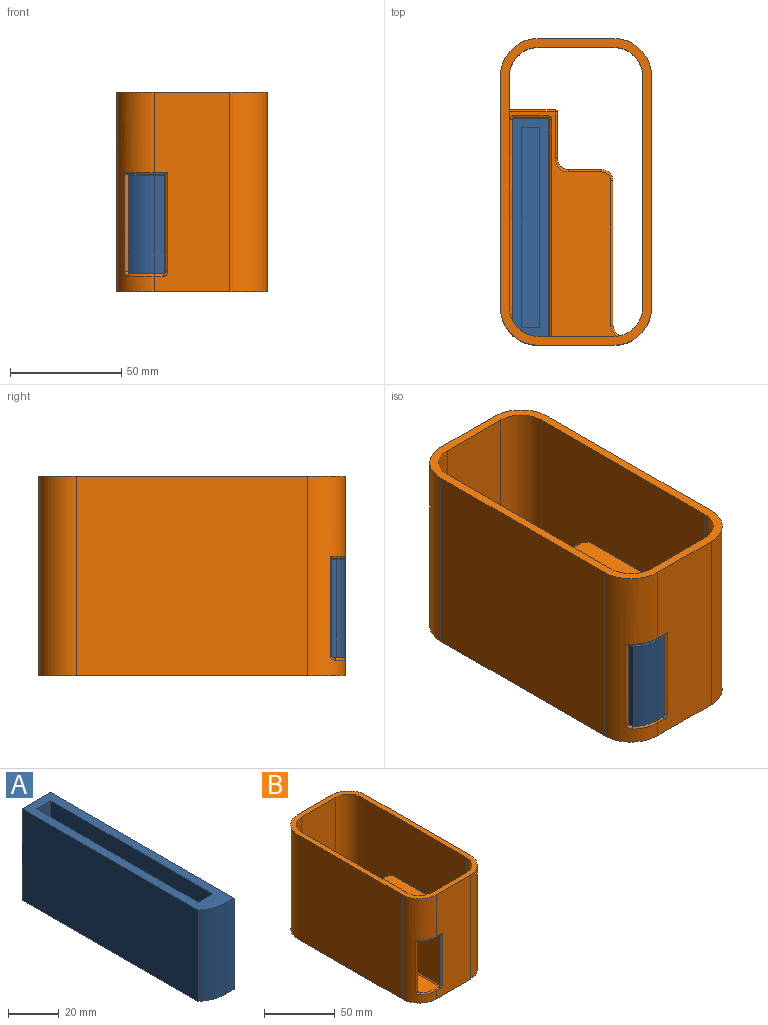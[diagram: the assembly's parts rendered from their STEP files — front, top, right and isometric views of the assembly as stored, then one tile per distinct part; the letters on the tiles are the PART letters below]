
ASSEMBLY  parts=2 mates=1
PART A: 13 faces, bbox 16x102x44 mm
  f0: plane 102x16mm, normal (0,0,1), area 896.4mm2, adj f2,f3,f4,f5,f7,f8,f9,f10
  f1: plane 102x16mm, normal (0,0,-1), area 1616.4mm2, adj f2,f3,f4,f5,f11,f12
  f2: plane 44x16mm, normal (0,1,0), area 704mm2, adj f0,f1,f4,f5
  f3: plane 44x0.43mm, normal (0,-1,0), area 18.9mm2, adj f0,f1,f5,f12
  f4: plane 102x44mm, normal (1,0,0), area 4488mm2, adj f0,f1,f2,f11
  f5: plane 98x44mm, normal (-1,0,0), area 4312mm2, adj f0,f1,f2,f3
  f6: plane 90x8mm, normal (0,0,1), area 720mm2, adj f7,f8,f9,f10
  f7: plane 40x8mm, normal (0,-1,0), area 320mm2, adj f0,f6,f9,f10
  f8: plane 40x8mm, normal (0,1,0), area 320mm2, adj f0,f6,f9,f10
  f9: plane 90x40mm, normal (-1,0,0), area 3600mm2, adj f0,f6,f7,f8
  f10: plane 90x40mm, normal (1,0,0), area 3600mm2, adj f0,f6,f7,f8
  f11: plane 44x4.62mm, normal (0,-1,0), area 203.1mm2, adj f0,f1,f4,f12
  f12: cylinder r=17mm len=44mm, axis (0,0,-1), area 523.8mm2, adj f0,f1,f3,f11
PART B: 81 faces, bbox 68.4x139.8x90.4 mm
  f0: plane 38.52x34mm, normal (0,1,0), area 1268.7mm2, adj f3,f4,f7,f20,f24,f40,f80
  f1: plane 101x50.48mm, normal (1,0,0), area 3978.9mm2, adj f2,f30,f31,f48,f49,f57
  f2: plane 36.48x25.38mm, normal (0,1,0), area 926.1mm2, adj f1,f20,f32,f67
  f3: plane 101x48.21mm, normal (0,0,1), area 2070.9mm2, adj f0,f4,f19,f20,f40,f43,f44,f45
  f4: cylinder r=13mm len=38.52mm, axis (0,0,-1), area 747.1mm2, adj f0,f3,f7,f19,f21,f43,f79
  f5: cylinder r=17mm len=90mm, axis (0,0,-1), area 1670mm2, adj f6,f7,f8,f13,f59,f60,f61,f63
  f6: plane 90x34mm, normal (0,-1,0), area 2779.3mm2, adj f5,f7,f8,f14,f62,f64,f65,f66
  f7: plane 138x68mm, normal (0,0,1), area 1481mm2, adj f0,f4,f5,f6,f9,f10,f11,f12
  f8: plane 138x68mm, normal (0,0,-1), area 3282.9mm2, adj f5,f6,f9,f10,f11,f12,f13,f14
  f9: plane 104x90mm, normal (1,0,0), area 9360mm2, adj f7,f8,f10,f14
  f10: cylinder r=17mm len=90mm, axis (0,0,-1), area 2403.3mm2, adj f7,f8,f9,f11
  f11: plane 90x34mm, normal (0,1,0), area 3060mm2, adj f7,f8,f10,f12
  f12: cylinder r=17mm len=90mm, axis (0,0,-1), area 2403.3mm2, adj f7,f8,f11,f13
  f13: plane 104x90mm, normal (-1,0,0), area 9360mm2, adj f5,f7,f8,f12
  f14: cylinder r=17mm len=90mm, axis (0,0,-1), area 2403.3mm2, adj f6,f7,f8,f9
  f15: plane 104x89mm, normal (-1,0,0), area 9256mm2, adj f7,f16,f20,f69
  f16: cylinder r=13mm len=89mm, axis (0,0,-1), area 1817.4mm2, adj f7,f15,f17,f70
  f17: plane 89x34mm, normal (0,-1,0), area 3026mm2, adj f7,f16,f18,f71
  f18: cylinder r=13mm len=89mm, axis (0,0,-1), area 1817.4mm2, adj f7,f17,f19,f72
  f19: plane 104x89mm, normal (1,0,0), area 4674.1mm2, adj f3,f4,f7,f18,f25,f47,f73
  f20: cylinder r=13mm len=89mm, axis (0,0,-1), area 1777.1mm2, adj f0,f2,f3,f7,f15,f32,f33,f52
  f21: plane 94.43x45.21mm, normal (1,0,0), area 3992.7mm2, adj f4,f22,f37,f42,f43,f61,f79
  f22: plane 17.17x8.44mm, normal (0,0,-1), area 37.4mm2, adj f21,f24,f61,f63,f65,f79,f80
  f23: plane 100.4x14.8mm, normal (0,0,1), area 1471.8mm2, adj f35,f36,f37,f60,f62
  f24: plane 100.4x44.8mm, normal (-1,0,0), area 4261.4mm2, adj f0,f22,f35,f40,f41,f66,f80
  f25: plane 50.48x20.62mm, normal (0,1,0), area 1040.7mm2, adj f19,f47,f49,f51
  f26: plane 42.4x14.8mm, normal (0,-1,0), area 627.5mm2, adj f36,f41,f42,f46
  f27: plane 65x8mm, normal (1,0,0), area 520mm2, adj f33,f34,f53,f75
  f28: plane 15x8mm, normal (0,1,0), area 120mm2, adj f30,f34,f55,f77
  f29: plane 69x19mm, normal (0,0,-1), area 1307.6mm2, adj f31,f32,f75,f76,f77
  f30: cylinder r=5mm len=14mm, axis (0,0,-1), area 80mm2, adj f1,f28,f56,f78
  f31: cylinder r=5mm len=80mm, axis (0,1,0), area 584mm2, adj f1,f29,f32,f78
  f32: cylinder r=5mm len=28.04mm, axis (-1,0,0), area 187.5mm2, adj f2,f20,f29,f31,f74
  f33: cylinder r=5mm len=11.89mm, axis (0,0,1), area 56.8mm2, adj f20,f27,f52,f74
  f34: cylinder r=5mm len=8mm, axis (0,0,-1), area 62.8mm2, adj f27,f28,f54,f76
  f35: cylinder r=1mm len=100.4mm, axis (0,1,0), area 157.7mm2, adj f23,f24,f38,f64
  f36: cylinder r=1mm len=14.8mm, axis (-1,0,0), area 23.2mm2, adj f23,f26,f38,f39
  f37: cylinder r=1mm len=96.22mm, axis (0,-1,0), area 149.4mm2, adj f21,f23,f39,f59
  f38: sphere r=1mm, area 1mm2, adj f35,f36,f41
  f39: sphere r=1mm, area 2.1mm2, adj f36,f37,f42
  f40: cylinder r=1mm len=97.4mm, axis (0,1,0), area 153mm2, adj f0,f3,f24,f44
  f41: cylinder r=1mm len=42.4mm, axis (0,0,1), area 66.6mm2, adj f24,f26,f38,f44
  f42: cylinder r=1mm len=42.4mm, axis (0,0,-1), area 66.6mm2, adj f21,f26,f39,f45
  f43: cylinder r=1mm len=89.89mm, axis (0,1,0), area 138.7mm2, adj f3,f4,f21,f45
  f44: torus R=2mm, axis (0,0,-1), area 3.4mm2, adj f3,f40,f41,f46
  f45: torus R=2mm, axis (0,0,-1), area 3.4mm2, adj f3,f42,f43,f46
  f46: cylinder r=1mm len=14.8mm, axis (-1,0,0), area 23.2mm2, adj f3,f26,f44,f45
  f47: cylinder r=1mm len=20.62mm, axis (1,0,0), area 32.4mm2, adj f3,f19,f25,f58
  f48: cylinder r=1mm len=102mm, axis (0,1,0), area 159.4mm2, adj f1,f8,f50,f67
  f49: cylinder r=1mm len=50.48mm, axis (0,0,1), area 79.3mm2, adj f1,f25,f50,f58
  f50: sphere r=1mm, area 1mm2, adj f48,f49,f51
  f51: cylinder r=1mm len=21.62mm, axis (-1,0,0), area 33.2mm2, adj f8,f25,f50,f73
  f52: torus R=6mm, axis (0,0,-1), area 9.2mm2, adj f3,f20,f33,f53
  f53: cylinder r=1mm len=65mm, axis (0,-1,0), area 102.1mm2, adj f3,f27,f52,f54
  f54: torus R=4mm, axis (0,0,-1), area 11.4mm2, adj f3,f34,f53,f55
  f55: cylinder r=1mm len=15mm, axis (1,0,0), area 23.6mm2, adj f3,f28,f54,f56
  f56: torus R=6mm, axis (0,0,-1), area 13.2mm2, adj f3,f30,f55,f57
  f57: cylinder r=1mm len=21mm, axis (0,-1,0), area 33mm2, adj f1,f3,f56,f58
  f58: sphere r=1mm, area 1mm2, adj f47,f49,f57
  f59: bspline ~3.41x3.05mm, area 5.8mm2, adj f5,f37,f60,f61
  f60: torus R=16mm, axis (0,0,-1), area 19.3mm2, adj f5,f23,f59,f62
  f61: cylinder r=1mm len=44.8mm, axis (0,0,-1), area 110.1mm2, adj f5,f21,f22,f59,f63
  f62: cylinder r=1mm len=4.02mm, axis (-1,0,0), area 6.3mm2, adj f6,f23,f60,f64
  f63: torus R=16mm, axis (0,0,-1), area 23.4mm2, adj f5,f22,f61,f65
  f64: torus R=2mm, axis (0,-1,0), area 3.4mm2, adj f6,f35,f62,f66
  f65: cylinder r=1mm len=6.02mm, axis (1,0,0), area 8.7mm2, adj f6,f22,f63,f66
  f66: cylinder r=1mm len=44.8mm, axis (0,0,-1), area 69.6mm2, adj f6,f24,f64,f65
  f67: cylinder r=1mm len=26.38mm, axis (-1,0,0), area 40.7mm2, adj f2,f8,f48,f68
  f68: torus R=14mm, axis (0,0,1), area 33mm2, adj f8,f20,f67,f69
  f69: cylinder r=1mm len=104mm, axis (0,-1,0), area 163.4mm2, adj f8,f15,f68,f70
  f70: torus R=14mm, axis (0,0,1), area 33mm2, adj f8,f16,f69,f71
  f71: cylinder r=1mm len=34mm, axis (1,0,0), area 53.4mm2, adj f8,f17,f70,f72
  f72: torus R=14mm, axis (0,0,1), area 33mm2, adj f8,f18,f71,f73
  f73: cylinder r=1mm len=16mm, axis (0,1,0), area 24.3mm2, adj f8,f19,f51,f72
  f74: bspline ~5x4.71mm, area 8.2mm2, adj f20,f32,f33,f75
  f75: cylinder r=1mm len=65mm, axis (0,-1,0), area 102.1mm2, adj f27,f29,f74,f76
  f76: torus R=4mm, axis (0,0,1), area 11.4mm2, adj f29,f34,f75,f77
  f77: cylinder r=1mm len=15mm, axis (1,0,0), area 23.6mm2, adj f28,f29,f76,f78
  f78: bspline ~6x6mm, area 5.4mm2, adj f30,f31,f77
  f79: torus R=14mm, axis (0,0,-1), area 22.4mm2, adj f4,f21,f22,f80
  f80: cylinder r=1mm len=5.02mm, axis (-1,0,0), area 7.9mm2, adj f0,f22,f24,f79
PLACE A t=(1.62,-16,-14.52)mm
PLACE B t=(22,0,-2)mm fixed
MATE planar A.f3 <-> B.f0  axis (0,-1,0) through (-6.17,-65,-16.52)mm
